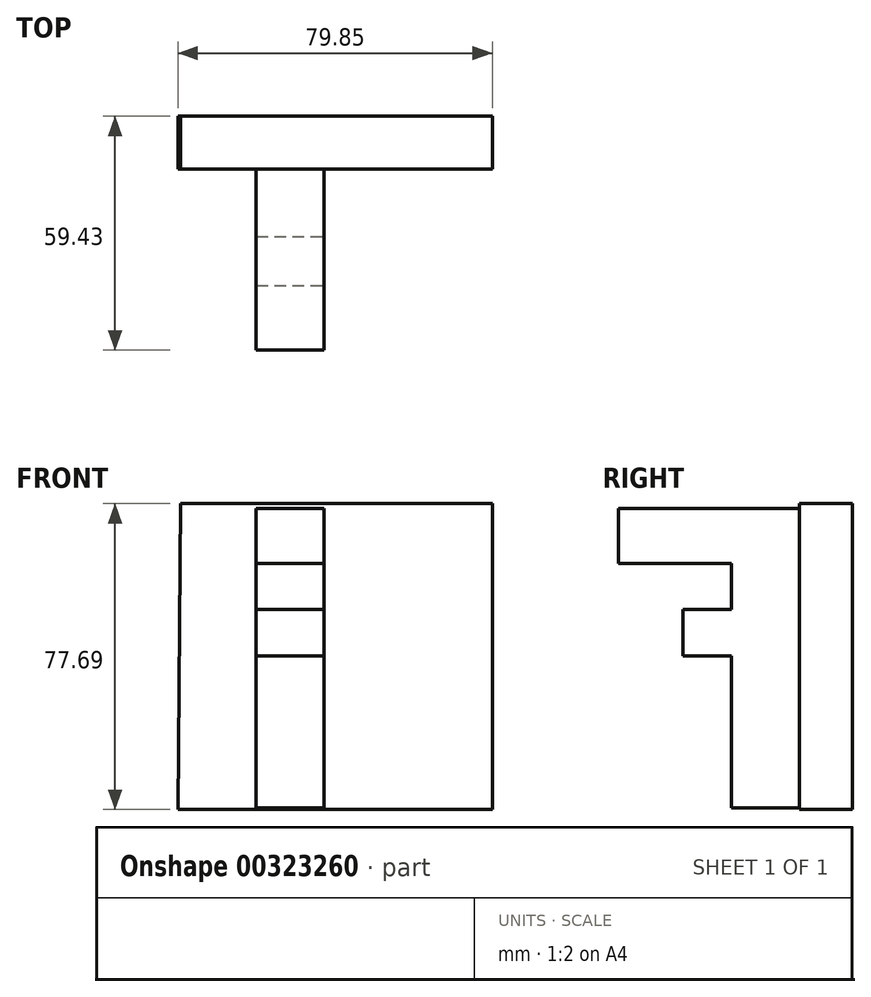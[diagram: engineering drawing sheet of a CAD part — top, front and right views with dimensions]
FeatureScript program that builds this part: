
annotation { "Feature Type Name" : "Feature", "Feature Type Description" : "" }
export const myFeature = defineFeature(function(context is Context, id is Id, definition is map)
    precondition{}
    {
        {
            var Q0;
            Q0=qCreatedBy(makeId("Front.planeOp"),FACE);
            var sketch = newSketch(context, id + "F0", { "sketchPlane" : qUnion([Q0])});
            skLineSegment(sketch, "E0", {"start": v(-36.52, 53.08) * mm, "end": v(42.71, 53.08) * mm});
            skLineSegment(sketch, "E1", {"start": v(42.71, 53.08) * mm, "end": v(42.71, -24.6) * mm});
            skLineSegment(sketch, "E2", {"start": v(42.71, -24.6) * mm, "end": v(-37.14, -24.6) * mm});
            skLineSegment(sketch, "E3", {"start": v(-37.14, -24.6) * mm, "end": v(-36.52, 53.08) * mm});
            skSolve(sketch);
        }
        {
            var Q0;
            Q0=makeQuery(id+"F0.imprint","IMPRINT",FACE,{"disambiguationData":[TD([[makeQuery(id+"F0.imprint","IMPRINT",EDGE,{"derivedFrom":sQuery(id+"F0.wireOp",EDGE,"E0")}),-1.0]])]});
            extrude(context, id + "F1", {"entities" : qUnion([Q0]), "depth" : 13.46 * mm});
        }
        {
            var Q0;
            Q0=qCreatedBy(makeId("Right.planeOp"),FACE);
            var sketch = newSketch(context, id + "F2", { "sketchPlane" : qUnion([Q0])});
            skLineSegment(sketch, "E4", {"start": v(-59.43, 51.84) * mm, "end": v(-12.38, 51.84) * mm});
            skLineSegment(sketch, "E5", {"start": v(-59.43, 51.84) * mm, "end": v(-59.43, 37.92) * mm});
            skLineSegment(sketch, "E6", {"start": v(-59.43, 37.92) * mm, "end": v(-30.64, 37.92) * mm});
            skLineSegment(sketch, "E7", {"start": v(-30.64, 37.92) * mm, "end": v(-30.64, 26.15) * mm});
            skLineSegment(sketch, "E8", {"start": v(-30.64, 26.15) * mm, "end": v(-43.02, 26.15) * mm});
            skLineSegment(sketch, "E9", {"start": v(-43.02, 26.15) * mm, "end": v(-43.02, 14.4) * mm});
            skLineSegment(sketch, "E10", {"start": v(-43.02, 14.4) * mm, "end": v(-30.64, 14.4) * mm});
            skLineSegment(sketch, "E11", {"start": v(-30.64, 14.4) * mm, "end": v(-30.64, -24.3) * mm});
            skLineSegment(sketch, "E12", {"start": v(-30.64, -24.3) * mm, "end": v(-12.38, -24.3) * mm});
            skLineSegment(sketch, "E13", {"start": v(-12.38, -24.3) * mm, "end": v(-12.38, 51.84) * mm});
            skSolve(sketch);
        }
        {
            var Q0;
            Q0=makeQuery(id+"F2.imprint","IMPRINT",FACE,{"disambiguationData":[TD([[makeQuery(id+"F2.imprint","IMPRINT",EDGE,{"derivedFrom":sQuery(id+"F2.wireOp",EDGE,"E4")}),-1.0]])]});
            extrude(context, id + "F3", {"entities" : qUnion([Q0]), "operationType" : NewBodyOperationType.ADD, "oppositeDirection" : true, "depth" : 17.27 * mm});
        }
    });
